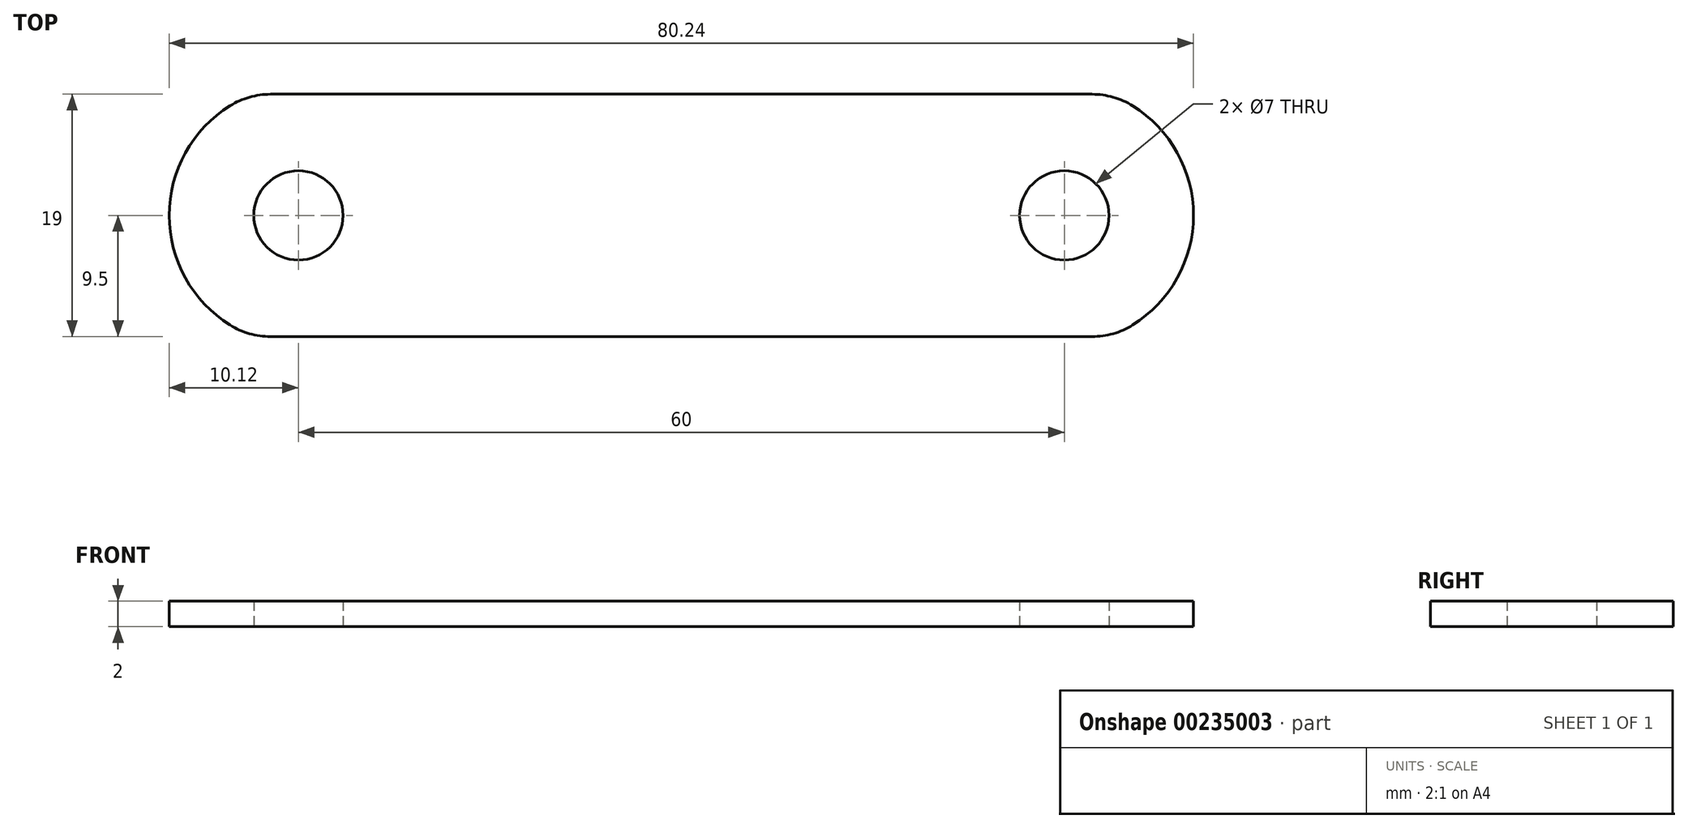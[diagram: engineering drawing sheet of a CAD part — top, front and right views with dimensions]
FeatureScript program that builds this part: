
annotation { "Feature Type Name" : "Feature", "Feature Type Description" : "" }
export const myFeature = defineFeature(function(context is Context, id is Id, definition is map)
    precondition{}
    {
        {
            var Q0;
            Q0=qCreatedBy(makeId("Top.planeOp"),FACE);
            var sketch = newSketch(context, id + "F0", { "sketchPlane" : qUnion([Q0])});
            skLineSegment(sketch, "E0", {"start": v(0, 0) * mm, "end": v(-33.5, 0) * mm});
            skLineSegment(sketch, "E1", {"start": v(-33.5, 19) * mm, "end": v(0, 19) * mm});
            skLineSegment(sketch, "E2", {"start": v(0, 19) * mm, "end": v(0, 0) * mm, "construction": true});
            skCircle(sketch, "E3", {"center": v(-30, 9.5) * mm, "radius": 3.5 * mm});
            skLineSegment(sketch, "E4.MirrorCS", {"start": v(0, 0) * mm, "end": v(33.5, 0) * mm});
            skLineSegment(sketch, "E5.MirrorCS", {"start": v(33.5, 19) * mm, "end": v(0, 19) * mm});
            skCircle(sketch, "E6.MirrorC", {"center": v(30, 9.5) * mm, "radius": 3.5 * mm});
            skLineSegment(sketch, "E7", {"start": v(-33.5, 19) * mm, "end": v(-33.5, 0) * mm, "construction": true});
            skArc(sketch, "E8", {"start": v(-33.5, 19) * mm, "mid": v(-40.12, 9.5) * mm, "end": v(-33.5, 0) * mm});
            skArc(sketch, "E9.MirrorCS", {"start": v(33.5, 19) * mm, "mid": v(40.12, 9.5) * mm, "end": v(33.5, 0) * mm});
            skSolve(sketch);
        }
        {
            var Q0;
            Q0=makeQuery(id+"F0.imprint","IMPRINT",FACE,{"disambiguationData":[TD([[makeQuery(id+"F0.imprint","IMPRINT",EDGE,{"derivedFrom":sQuery(id+"F0.wireOp",EDGE,"E0")}),-1.0]])]});
            extrude(context, id + "F1", {"entities" : qUnion([Q0]), "depth" : 2 * mm});
        }
        {
            var Q0;
            Q0=makeQuery(id+"F1.opExtrude","SWEPT_EDGE",EDGE,{"disambiguationData":[OSD([sQuery(id+"F0.wireOp",EDGE,"E0"),sQuery(id+"F0.wireOp",EDGE,"E8")])]});
            var Q1;
            Q1=makeQuery(id+"F1.opExtrude","SWEPT_EDGE",EDGE,{"disambiguationData":[OSD([sQuery(id+"F0.wireOp",EDGE,"E1"),sQuery(id+"F0.wireOp",EDGE,"E8")])]});
            var Q2;
            Q2=makeQuery(id+"F1.opExtrude","SWEPT_EDGE",EDGE,{"disambiguationData":[OSD([sQuery(id+"F0.wireOp",EDGE,"E5.MirrorCS"),sQuery(id+"F0.wireOp",EDGE,"E9.MirrorCS")])]});
            var Q3;
            Q3=makeQuery(id+"F1.opExtrude","SWEPT_EDGE",EDGE,{"disambiguationData":[OSD([sQuery(id+"F0.wireOp",EDGE,"E4.MirrorCS"),sQuery(id+"F0.wireOp",EDGE,"E9.MirrorCS")])]});
            fillet(context, id + "F2", {"entities" : qUnion([Q0, Q1, Q2, Q3]), "radius" : 6 * mm, "tangentPropagation" : true, "allowEdgeOverflow" : false});
        }
    });
